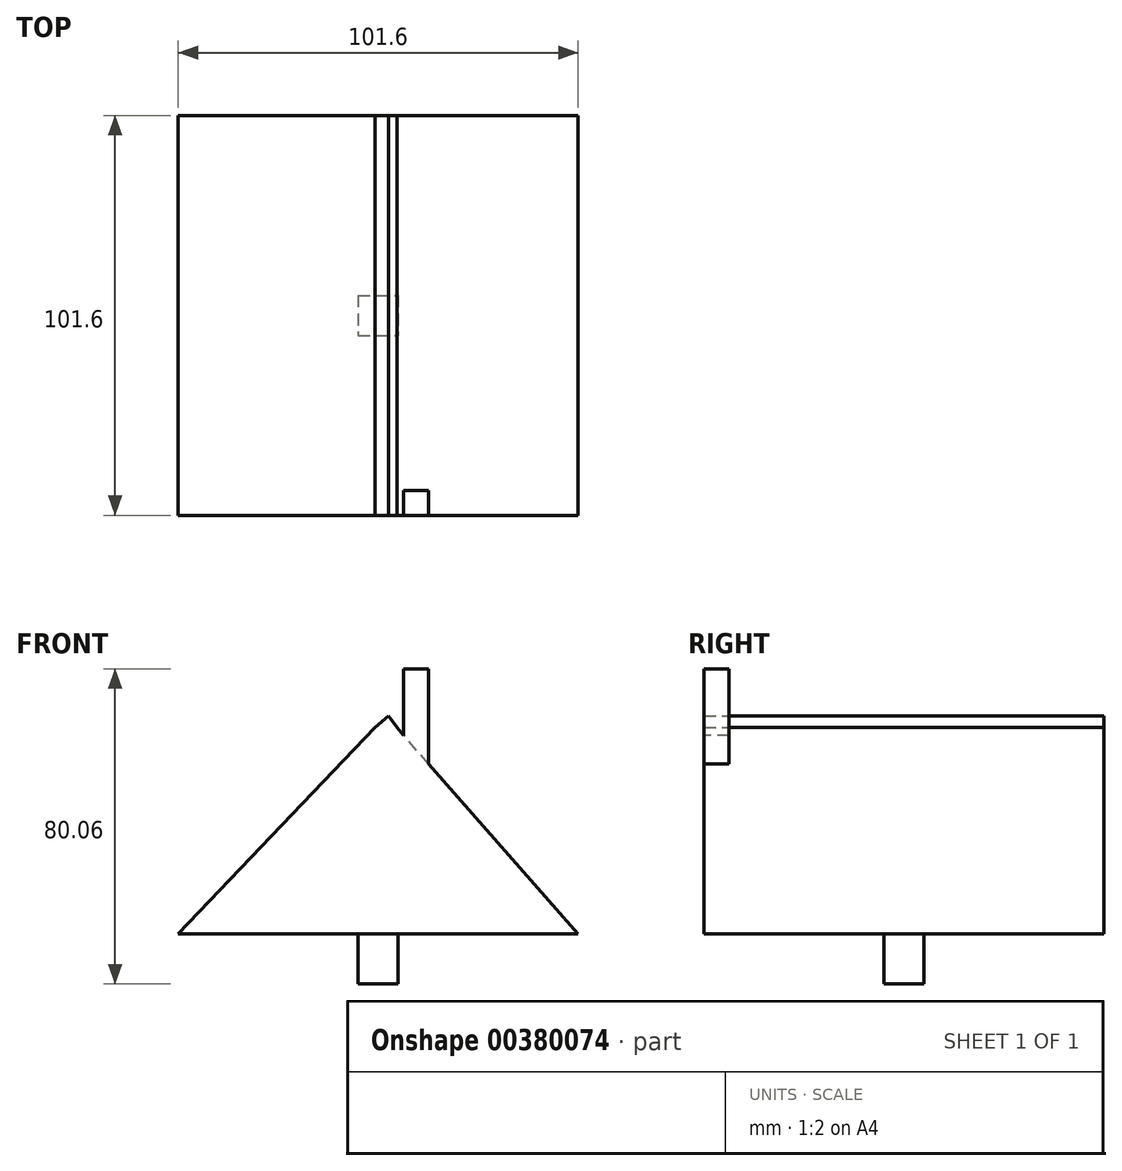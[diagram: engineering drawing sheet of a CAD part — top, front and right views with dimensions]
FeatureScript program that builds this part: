
annotation { "Feature Type Name" : "Feature", "Feature Type Description" : "" }
export const myFeature = defineFeature(function(context is Context, id is Id, definition is map)
    precondition{}
    {
        {
            var Q0;
            Q0=qCreatedBy(makeId("Front.planeOp"),FACE);
            var sketch = newSketch(context, id + "F0", { "sketchPlane" : qUnion([Q0])});
            skLineSegment(sketch, "E0", {"start": v(-53.38, -50.48) * mm, "end": v(48.22, -50.48) * mm});
            skLineSegment(sketch, "E1", {"start": v(-53.38, -50.48) * mm, "end": v(-3.4, 1.96) * mm});
            skLineSegment(sketch, "E2", {"start": v(48.22, -50.48) * mm, "end": v(2.2, 1.96) * mm});
            skLineSegment(sketch, "E3", {"start": v(-3.4, 1.96) * mm, "end": v(0, 4.94) * mm});
            skLineSegment(sketch, "E4", {"start": v(2.2, 1.96) * mm, "end": v(0, 4.94) * mm});
            skSolve(sketch);
        }
        {
            var Q0;
            Q0=makeQuery(id+"F0.imprint","IMPRINT",FACE,{"disambiguationData":[TD([[makeQuery(id+"F0.imprint","IMPRINT",EDGE,{"derivedFrom":sQuery(id+"F0.wireOp",EDGE,"E0")}),1.0]])]});
            extrude(context, id + "F1", {"entities" : qUnion([Q0]), "depth" : 101.6 * mm});
        }
        {
            var Q0;
            Q0=makeQuery(id+"F1.opExtrude","CAP_FACE",FACE,{"disambiguationData":[OSD([sQuery(id+"F0.wireOp",EDGE,"E0"),sQuery(id+"F0.wireOp",EDGE,"E1"),sQuery(id+"F0.wireOp",EDGE,"E2"),sQuery(id+"F0.wireOp",EDGE,"E3"),sQuery(id+"F0.wireOp",EDGE,"E4")])],"isStart":false});
            var sketch = newSketch(context, id + "F2", { "sketchPlane" : qUnion([Q0])});
            skLineSegment(sketch, "E5", {"start": v(3.92, 0) * mm, "end": v(3.92, 16.88) * mm});
            skLineSegment(sketch, "E6", {"start": v(3.92, 16.88) * mm, "end": v(10.27, 16.88) * mm});
            skLineSegment(sketch, "E7", {"start": v(10.27, 16.88) * mm, "end": v(10.27, -7.24) * mm});
            skSolve(sketch);
        }
        {
            var Q0;
            {var subQ0=sQuery(id+"F2.wireOp",EDGE,"E5");Q0=makeQuery(id+"F2.imprint","IMPRINT",FACE,{"disambiguationData":[TD([[makeQuery(id+"F2.imprint","IMPRINT",EDGE,{"derivedFrom":subQ0}),-1.0]])]});}
            extrude(context, id + "F3", {"entities" : qUnion([Q0]), "operationType" : NewBodyOperationType.ADD, "oppositeDirection" : true, "depth" : 6.35 * mm});
        }
        {
            var Q0;
            Q0=makeQuery(id+"F1.opExtrude","SWEPT_FACE",FACE,{"disambiguationData":[OSD([sQuery(id+"F0.wireOp",EDGE,"E0")])]});
            var sketch = newSketch(context, id + "F4", { "sketchPlane" : qUnion([Q0])});
            skLineSegment(sketch, "E8.bottom", {"start": v(2.5, 55.88) * mm, "end": v(-7.66, 55.88) * mm});
            skLineSegment(sketch, "E8.top", {"start": v(2.5, 45.72) * mm, "end": v(-7.66, 45.72) * mm});
            skLineSegment(sketch, "E8.left", {"start": v(2.5, 55.88) * mm, "end": v(2.5, 45.72) * mm});
            skLineSegment(sketch, "E8.right", {"start": v(-7.66, 55.88) * mm, "end": v(-7.66, 45.72) * mm});
            skPoint(sketch, "E8.middle", {"position": v(-2.58, 50.8) * mm});
            skSolve(sketch);
        }
        {
            var Q0;
            Q0=makeQuery(id+"F4.imprint","IMPRINT",FACE,{"disambiguationData":[TD([[makeQuery(id+"F4.imprint","IMPRINT",EDGE,{"derivedFrom":sQuery(id+"F4.wireOp",EDGE,"E8.bottom")}),1.0]])]});
            extrude(context, id + "F5", {"entities" : qUnion([Q0]), "operationType" : NewBodyOperationType.ADD, "depth" : -12.7 * mm});
        }
        {
            var Q0;
            Q0=makeQuery(id+"F1.opExtrude","SWEPT_FACE",FACE,{"disambiguationData":[OSD([sQuery(id+"F0.wireOp",EDGE,"E0")])]});
            var sketch = newSketch(context, id + "F6", { "sketchPlane" : qUnion([Q0])});
            skLineSegment(sketch, "E9.bottom", {"start": v(-7.66, 45.72) * mm, "end": v(2.5, 45.72) * mm});
            skLineSegment(sketch, "E9.top", {"start": v(-7.66, 55.88) * mm, "end": v(2.5, 55.88) * mm});
            skLineSegment(sketch, "E9.left", {"start": v(-7.66, 45.72) * mm, "end": v(-7.66, 55.88) * mm});
            skLineSegment(sketch, "E9.right", {"start": v(2.5, 45.72) * mm, "end": v(2.5, 55.88) * mm});
            skPoint(sketch, "E9.middle", {"position": v(-2.58, 50.8) * mm});
            skSolve(sketch);
        }
        {
            var Q0;
            Q0 = qSketchRegion(id + "F6", true);
            extrude(context, id + "F7", {"entities" : qUnion([Q0]), "operationType" : NewBodyOperationType.ADD, "depth" : 12.7 * mm});
        }
    });
